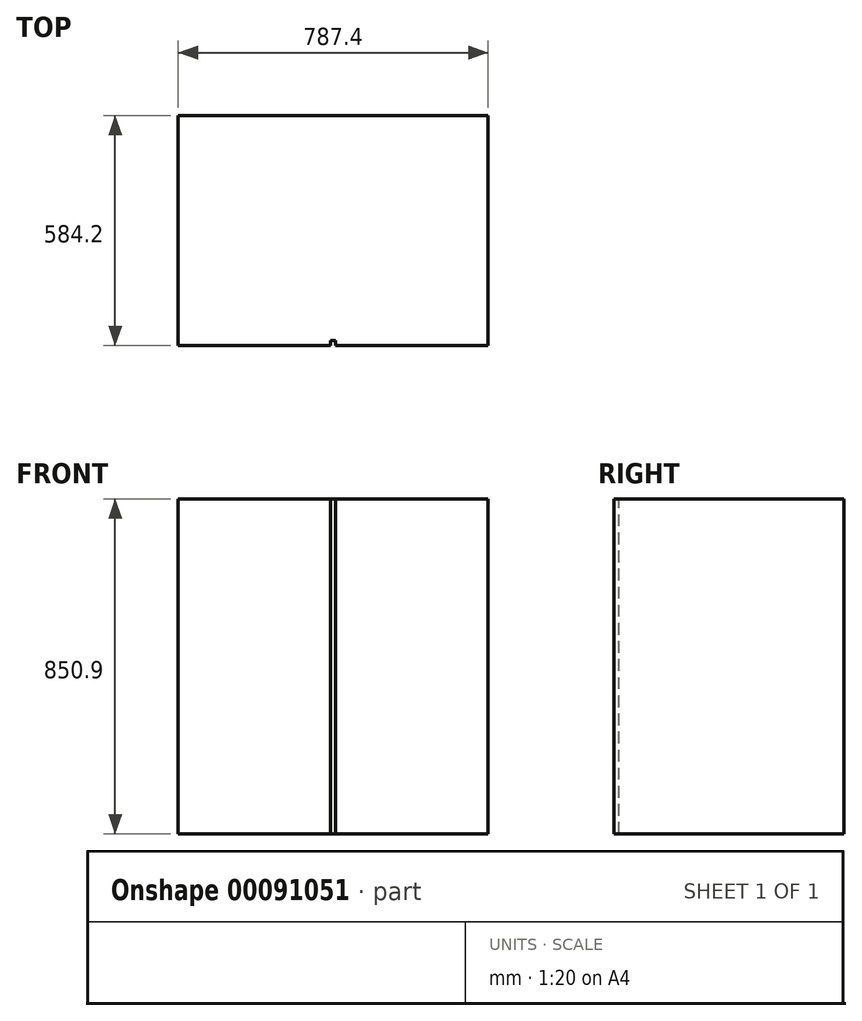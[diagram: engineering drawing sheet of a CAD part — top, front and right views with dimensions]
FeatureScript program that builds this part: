
annotation { "Feature Type Name" : "Feature", "Feature Type Description" : "" }
export const myFeature = defineFeature(function(context is Context, id is Id, definition is map)
    precondition{}
    {
        {
            var Q0;
            Q0=qCreatedBy(makeId("Top.planeOp"),FACE);
            var sketch = newSketch(context, id + "F0", { "sketchPlane" : qUnion([Q0])});
            skLineSegment(sketch, "E0.bottom", {"start": v(-390.8, 191.41) * mm, "end": v(396.6, 191.41) * mm});
            skLineSegment(sketch, "E0.top", {"start": v(-390.8, -392.79) * mm, "end": v(396.6, -392.79) * mm});
            skLineSegment(sketch, "E0.left", {"start": v(-390.8, 191.41) * mm, "end": v(-390.8, -392.79) * mm});
            skLineSegment(sketch, "E0.right", {"start": v(396.6, 191.41) * mm, "end": v(396.6, -392.79) * mm});
            skSolve(sketch);
        }
        {
            var Q0;
            Q0 = qSketchRegion(id + "F0", true);
            extrude(context, id + "F1", {"entities" : qUnion([Q0]), "depth" : 850.9 * mm});
        }
        {
            var Q0;
            Q0=makeQuery(id+"F1.opExtrude","CAP_FACE",FACE,{"disambiguationData":[OSD([sQuery(id+"F0.wireOp",EDGE,"E0.bottom"),sQuery(id+"F0.wireOp",EDGE,"E0.top"),sQuery(id+"F0.wireOp",EDGE,"E0.left"),sQuery(id+"F0.wireOp",EDGE,"E0.right")])],"isStart":false});
            var sketch = newSketch(context, id + "F2", { "sketchPlane" : qUnion([Q0])});
            skLineSegment(sketch, "E1", {"start": v(-3.45, -392.79) * mm, "end": v(-3.45, -380.09) * mm});
            skLineSegment(sketch, "E2", {"start": v(-3.45, -380.09) * mm, "end": v(9.25, -380.09) * mm});
            skLineSegment(sketch, "E3", {"start": v(9.25, -380.09) * mm, "end": v(9.25, -392.79) * mm});
            skLineSegment(sketch, "E4", {"start": v(9.25, -392.79) * mm, "end": v(-3.45, -392.79) * mm});
            skPoint(sketch, "E5", {"position": v(2.9, -380.09) * mm});
            skPoint(sketch, "E6", {"position": v(2.9, -392.79) * mm});
            skSolve(sketch);
        }
        {
            var Q0;
            Q0 = qSketchRegion(id + "F2", true);
            extrude(context, id + "F3", {"entities" : qUnion([Q0]), "operationType" : NewBodyOperationType.REMOVE, "endBound" : BoundingType.THROUGH_ALL, "oppositeDirection" : true, "depth" : 25.4 * mm});
        }
    });
